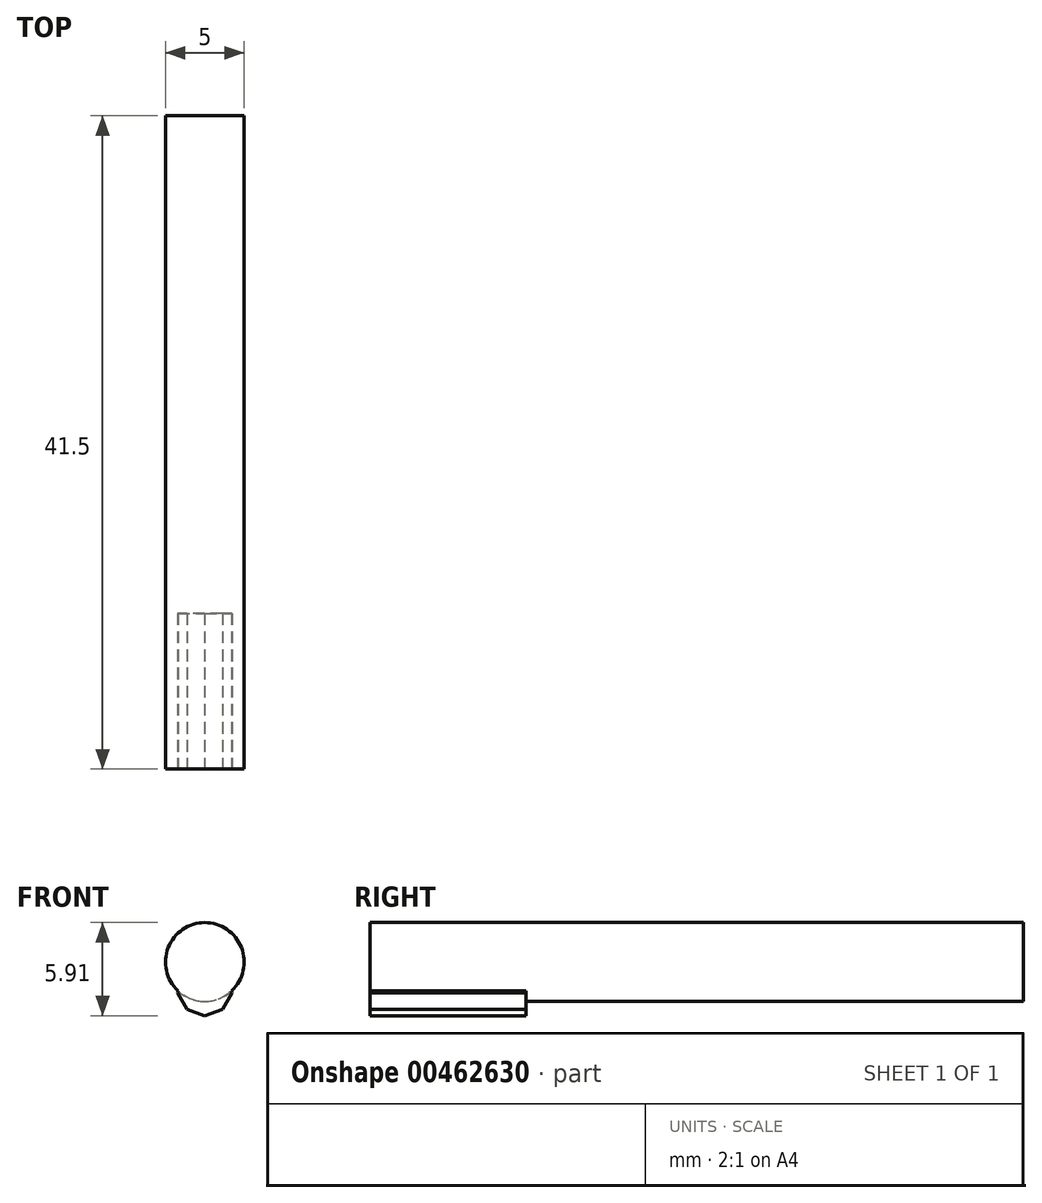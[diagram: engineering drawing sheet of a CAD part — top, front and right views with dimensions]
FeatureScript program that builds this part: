
annotation { "Feature Type Name" : "Feature", "Feature Type Description" : "" }
export const myFeature = defineFeature(function(context is Context, id is Id, definition is map)
    precondition{}
    {
        {
            var Q0;
            Q0=qCreatedBy(makeId("Front.planeOp"),FACE);
            var sketch = newSketch(context, id + "F0", { "sketchPlane" : qUnion([Q0])});
            skCircle(sketch, "E0", {"center": v(0, 0) * mm, "radius": 2.5 * mm});
            skSolve(sketch);
        }
        {
            var Q0;
            Q0=makeQuery(id+"F0.imprint","IMPRINT",FACE,{"disambiguationData":[TD([[makeQuery(id+"F0.imprint","IMPRINT",EDGE,{"derivedFrom":sQuery(id+"F0.wireOp",EDGE,"E0")}),1.0]])]});
            extrude(context, id + "F1", {"entities" : qUnion([Q0]), "endBound" : BoundingType.SYMMETRIC, "oppositeDirection" : true, "depth" : 41.5 * mm});
        }
        {
            var Q0;
            Q0=makeQuery(id+"F1.opExtrude","CAP_FACE",FACE,{"disambiguationData":[OSD([sQuery(id+"F0.wireOp",EDGE,"E0")])],"isStart":true});
            var sketch = newSketch(context, id + "F2", { "sketchPlane" : qUnion([Q0])});
            skCircle(sketch, "E1", {"center": v(0, 0) * mm, "radius": 1.65 * mm});
            skCircle(sketch, "E2.cCircle", {"center": v(0, -1.65) * mm, "radius": 1.65 * mm, "construction": true});
            skLineSegment(sketch, "E2.0", {"start": v(-0.6, 0) * mm, "end": v(0.6, 0) * mm});
            skLineSegment(sketch, "E2.1", {"start": v(0.6, 0) * mm, "end": v(1.52, -0.77) * mm});
            skLineSegment(sketch, "E2.2", {"start": v(1.52, -0.77) * mm, "end": v(1.73, -1.96) * mm});
            skLineSegment(sketch, "E2.3", {"start": v(1.73, -1.96) * mm, "end": v(1.13, -3) * mm});
            skLineSegment(sketch, "E2.4", {"start": v(1.13, -3) * mm, "end": v(0, -3.41) * mm});
            skLineSegment(sketch, "E2.5", {"start": v(0, -3.41) * mm, "end": v(-1.13, -3) * mm});
            skLineSegment(sketch, "E2.6", {"start": v(-1.13, -3) * mm, "end": v(-1.73, -1.96) * mm});
            skLineSegment(sketch, "E2.7", {"start": v(-1.73, -1.96) * mm, "end": v(-1.52, -0.77) * mm});
            skLineSegment(sketch, "E2.8", {"start": v(-1.52, -0.77) * mm, "end": v(-0.6, 0) * mm});
            skCircle(sketch, "E3.cCircle", {"center": v(0, 0) * mm, "radius": 1.65 * mm, "construction": true});
            skLineSegment(sketch, "E3.0", {"start": v(-1.2, 1.65) * mm, "end": v(1.2, 1.65) * mm});
            skLineSegment(sketch, "E3.1", {"start": v(1.2, 1.65) * mm, "end": v(1.94, -0.63) * mm});
            skLineSegment(sketch, "E3.2", {"start": v(1.94, -0.63) * mm, "end": v(0, -2.04) * mm});
            skLineSegment(sketch, "E3.3", {"start": v(0, -2.04) * mm, "end": v(-1.94, -0.63) * mm});
            skLineSegment(sketch, "E3.4", {"start": v(-1.94, -0.63) * mm, "end": v(-1.2, 1.65) * mm});
            skPoint(sketch, "E3.0.midPoint", {"position": v(0, 1.65) * mm});
            skSolve(sketch);
        }
        {
            var Q0;
            {var subQ12=sQuery(id+"F2.wireOp",EDGE,"E2.3");Q0=makeQuery(id+"F2.imprint","IMPRINT",FACE,{"disambiguationData":[TD([[makeQuery(id+"F2.imprint","IMPRINT",EDGE,{"derivedFrom":subQ12}),1.0]])]});}
            var Q1;
            {var subQ8=sQuery(id+"F2.wireOp",EDGE,"E2.0");Q1=makeQuery(id+"F2.imprint","IMPRINT",FACE,{"disambiguationData":[TD([[makeQuery(id+"F2.imprint","IMPRINT",EDGE,{"derivedFrom":subQ8}),1.0]])]});}
            var Q2;
            {var subQ5=sQuery(id+"F2.wireOp",EDGE,"E2.3");Q2=makeQuery(id+"F2.imprint","IMPRINT",FACE,{"disambiguationData":[TD([[makeQuery(id+"F2.imprint","IMPRINT",EDGE,{"derivedFrom":subQ5}),-1.0]])]});}
            var Q3;
            {var subQ0=sQuery(id+"F2.wireOp",EDGE,"E2.0");Q3=makeQuery(id+"F2.imprint","IMPRINT",FACE,{"disambiguationData":[TD([[makeQuery(id+"F2.imprint","IMPRINT",EDGE,{"derivedFrom":subQ0}),-1.0]])]});}
            var Q4;
            {var subQ1=sQuery(id+"F2.wireOp",EDGE,"E3.1");var subQ3=sQuery(id+"F2.wireOp",EDGE,"E1");var subQ4=makeQuery(id+"F2.imprint","INTERSECT",VERTEX,{"derivedFrom":[subQ3,subQ1]});Q4=makeQuery(id+"F2.imprint","IMPRINT",FACE,{"disambiguationData":[TD([[makeQuery(id+"F2.imprint","IMPRINT",EDGE,{"disambiguationData":[TD([[subQ4,1.0]])],"derivedFrom":subQ3}),-1.0]])]});}
            var Q5;
            Q5=makeQuery(id+"F1.opExtrude","CAP_FACE",FACE,{"disambiguationData":[OSD([sQuery(id+"F0.wireOp",EDGE,"E0")])],"isStart":true});
            var Q6;
            {var subQ0=sQuery(id+"F2.wireOp",EDGE,"E3.4");var subQ7=sQuery(id+"F2.wireOp",EDGE,"E1");var subQ9=makeQuery(id+"F2.imprint","INTERSECT",VERTEX,{"derivedFrom":[subQ7,subQ0]});Q6=makeQuery(id+"F2.imprint","IMPRINT",FACE,{"disambiguationData":[TD([[makeQuery(id+"F2.imprint","IMPRINT",EDGE,{"disambiguationData":[TD([[subQ9,-1.0]])],"derivedFrom":subQ7}),-1.0]])]});}
            var Q7;
            {var subQ0=sQuery(id+"F2.wireOp",EDGE,"E3.3");var subQ1=sQuery(id+"F2.wireOp",EDGE,"E1");var subQ2=makeQuery(id+"F2.imprint","INTERSECT",VERTEX,{"derivedFrom":[subQ1,subQ0]});Q7=makeQuery(id+"F2.imprint","IMPRINT",FACE,{"disambiguationData":[TD([[makeQuery(id+"F2.imprint","IMPRINT",EDGE,{"disambiguationData":[TD([[subQ2,-1.0]])],"derivedFrom":subQ1}),-1.0]])]});}
            var Q8;
            {var subQ0=sQuery(id+"F2.wireOp",EDGE,"E3.0");var subQ1=sQuery(id+"F2.wireOp",EDGE,"E1");var subQ2=makeQuery(id+"F2.imprint","INTERSECT",VERTEX,{"derivedFrom":[subQ1,subQ0]});Q8=makeQuery(id+"F2.imprint","IMPRINT",FACE,{"disambiguationData":[TD([[makeQuery(id+"F2.imprint","IMPRINT",EDGE,{"disambiguationData":[TD([[subQ2,-1.0]])],"derivedFrom":subQ1}),-1.0]])]});}
            var Q9;
            {var subQ0=sQuery(id+"F2.wireOp",EDGE,"E3.0");var subQ1=sQuery(id+"F2.wireOp",EDGE,"E1");var subQ2=makeQuery(id+"F2.imprint","INTERSECT",VERTEX,{"derivedFrom":[subQ1,subQ0]});Q9=makeQuery(id+"F2.imprint","IMPRINT",FACE,{"disambiguationData":[TD([[makeQuery(id+"F2.imprint","IMPRINT",EDGE,{"disambiguationData":[TD([[subQ2,1.0]])],"derivedFrom":subQ1}),-1.0]])]});}
            var Q10;
            {var subQ0=sQuery(id+"F2.wireOp",EDGE,"E3.2");var subQ1=sQuery(id+"F2.wireOp",EDGE,"E1");var subQ2=makeQuery(id+"F2.imprint","INTERSECT",VERTEX,{"derivedFrom":[subQ1,subQ0]});Q10=makeQuery(id+"F2.imprint","IMPRINT",FACE,{"disambiguationData":[TD([[makeQuery(id+"F2.imprint","IMPRINT",EDGE,{"disambiguationData":[TD([[subQ2,-1.0]])],"derivedFrom":subQ1}),-1.0]])]});}
            var Q11;
            {var subQ0=sQuery(id+"F2.wireOp",EDGE,"E2.8");var subQ1=sQuery(id+"F2.wireOp",EDGE,"E1");var subQ2=makeQuery(id+"F2.imprint","INTERSECT",VERTEX,{"derivedFrom":[subQ1,subQ0]});Q11=makeQuery(id+"F2.imprint","IMPRINT",FACE,{"disambiguationData":[TD([[makeQuery(id+"F2.imprint","IMPRINT",EDGE,{"disambiguationData":[TD([[subQ2,-1.0]])],"derivedFrom":subQ1}),-1.0]])]});}
            extrude(context, id + "F3", {"entities" : qUnion([Q0, Q1, Q2, Q3, Q4, Q5, Q6, Q7, Q8, Q9, Q10, Q11]), "operationType" : NewBodyOperationType.ADD, "oppositeDirection" : true, "depth" : 9.9 * mm});
        }
    });
